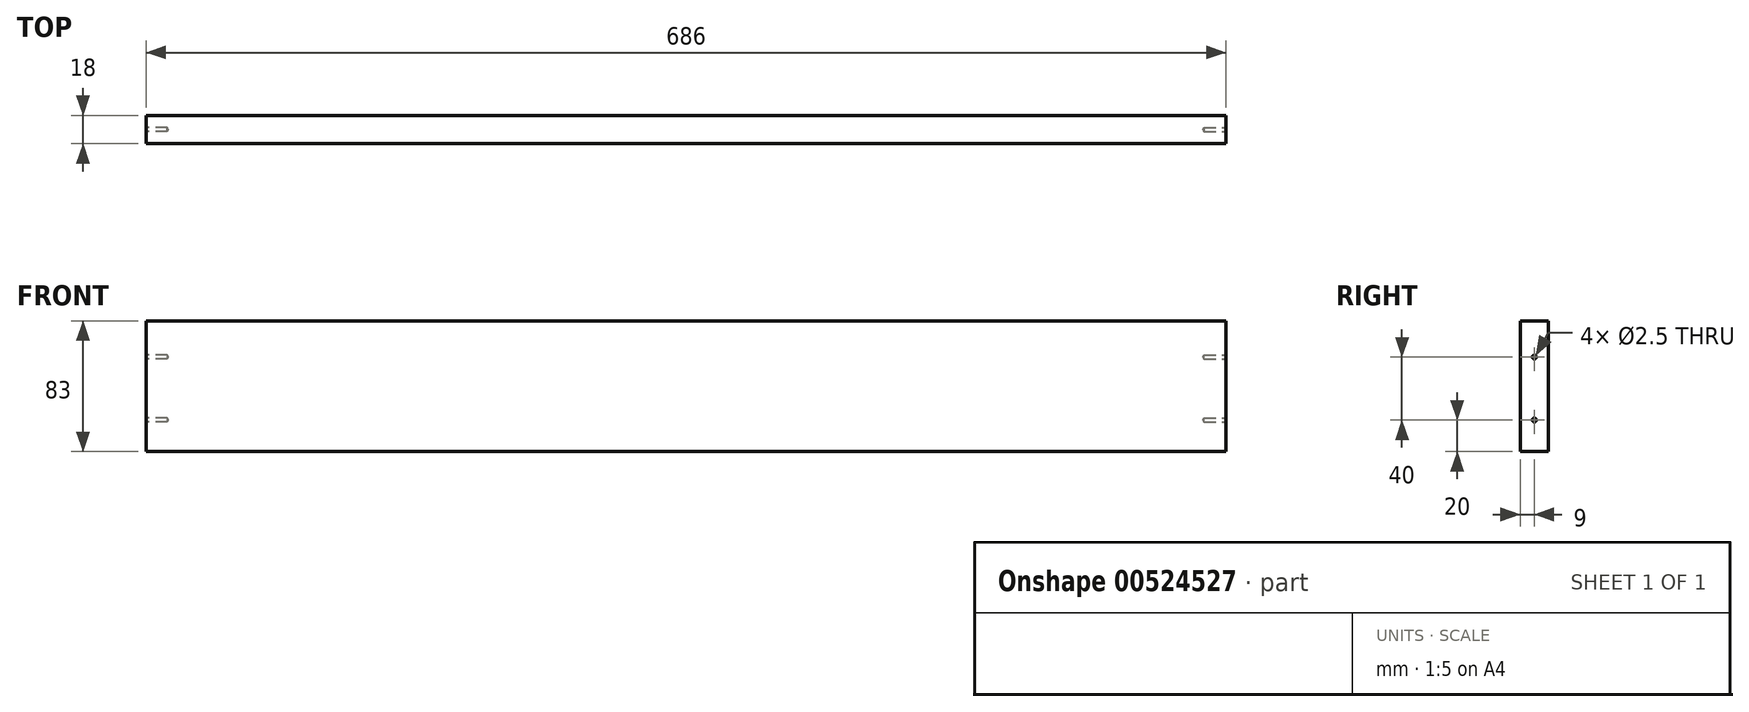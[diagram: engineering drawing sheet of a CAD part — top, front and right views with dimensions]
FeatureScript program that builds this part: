
annotation { "Feature Type Name" : "Feature", "Feature Type Description" : "" }
export const myFeature = defineFeature(function(context is Context, id is Id, definition is map)
    precondition{}
    {
        {
            var Q0;
            Q0=qCreatedBy(makeId("Front.planeOp"),FACE);
            var sketch = newSketch(context, id + "F0", { "sketchPlane" : qUnion([Q0])});
            skLineSegment(sketch, "E0.bottom", {"start": v(0, 0) * mm, "end": v(686, 0) * mm});
            skLineSegment(sketch, "E0.top", {"start": v(0, 83) * mm, "end": v(686, 83) * mm});
            skLineSegment(sketch, "E0.left", {"start": v(0, 0) * mm, "end": v(0, 83) * mm});
            skLineSegment(sketch, "E0.right", {"start": v(686, 0) * mm, "end": v(686, 83) * mm});
            skSolve(sketch);
        }
        {
            var Q0;
            Q0=qSketchRegion(id+"F0",true);
            extrude(context, id + "F1", {"entities" : qUnion([Q0]), "depth" : 18 * mm, "offsetDistance" : 25 * mm});
        }
        {
            var Q0;
            Q0=makeQuery(id+"F1.opExtrude","SWEPT_FACE",FACE,{"disambiguationData":[OSD([sQuery(id+"F0.wireOp",EDGE,"E0.left")])]});
            var sketch = newSketch(context, id + "F2", { "sketchPlane" : qUnion([Q0])});
            skPoint(sketch, "E1", {"position": v(9, 20) * mm});
            skPoint(sketch, "E2", {"position": v(9, 60) * mm});
            skSolve(sketch);
        }
        {
            var Q0;
            Q0=sQuery(id+"F2.wireOp",VERTEX,"E1");
            var Q1;
            Q1=sQuery(id+"F2.wireOp",VERTEX,"E2");
            var Q2;
            Q2=makeQuery(id+"F1.opExtrude","SWEPT_BODY",BODY,{"disambiguationData":[OSD([sQuery(id+"F0.wireOp",EDGE,"E0.bottom"),sQuery(id+"F0.wireOp",EDGE,"E0.top"),sQuery(id+"F0.wireOp",EDGE,"E0.left"),sQuery(id+"F0.wireOp",EDGE,"E0.right")])]});
            hole(context, id + "F3", {"style" : HoleStyle.SIMPLE, "endStyle" : HoleEndStyle.BLIND, "standardTappedOrClearance" : lookupTablePath({ "standard" : "ISO", "engagement" : "75%", "pitch" : "0.5 mm", "size" : "M3", "type" : "Tapped" }), "standardBlindInLast" : lookupTablePath({ "standard" : "ISO", "engagement" : "75%", "pitch" : "0.5 mm", "size" : "M3", "type" : "Tapped" }), "holeDiameter" : 2.5 * mm, "showTappedDepth" : true, "holeDepth" : 13.5 * mm, "isTappedThrough" : true, "tappedDepth" : 12 * mm, "tapClearance" : 3, "locations" : qUnion([Q0, Q1]), "scope" : qUnion([Q2]), "majorDiameter" : 3 * mm});
        }
        {
            var Q0;
            Q0=makeQuery(id+"F1.opExtrude","SWEPT_FACE",FACE,{"disambiguationData":[OSD([sQuery(id+"F0.wireOp",EDGE,"E0.right")])]});
            var sketch = newSketch(context, id + "F4", { "sketchPlane" : qUnion([Q0])});
            skPoint(sketch, "E3", {"position": v(-9, 20) * mm});
            skPoint(sketch, "E4", {"position": v(-9, 60) * mm});
            skSolve(sketch);
        }
        {
            var Q0;
            Q0=sQuery(id+"F4.wireOp",VERTEX,"E3");
            var Q1;
            Q1=sQuery(id+"F4.wireOp",VERTEX,"E4");
            var Q2;
            Q2=makeQuery(id+"F1.opExtrude","SWEPT_BODY",BODY,{"disambiguationData":[OSD([sQuery(id+"F0.wireOp",EDGE,"E0.bottom"),sQuery(id+"F0.wireOp",EDGE,"E0.top"),sQuery(id+"F0.wireOp",EDGE,"E0.left"),sQuery(id+"F0.wireOp",EDGE,"E0.right")])]});
            hole(context, id + "F5", {"style" : HoleStyle.SIMPLE, "endStyle" : HoleEndStyle.BLIND, "standardTappedOrClearance" : lookupTablePath({ "standard" : "ISO", "engagement" : "75%", "pitch" : "0.5 mm", "size" : "M3", "type" : "Tapped" }), "standardBlindInLast" : lookupTablePath({ "standard" : "ISO", "engagement" : "75%", "pitch" : "0.5 mm", "size" : "M3", "type" : "Tapped" }), "holeDiameter" : 2.5 * mm, "showTappedDepth" : true, "holeDepth" : 14 * mm, "isTappedThrough" : true, "tappedDepth" : 12.5 * mm, "tapClearance" : 3, "locations" : qUnion([Q0, Q1]), "scope" : qUnion([Q2]), "majorDiameter" : 3 * mm});
        }
    });
